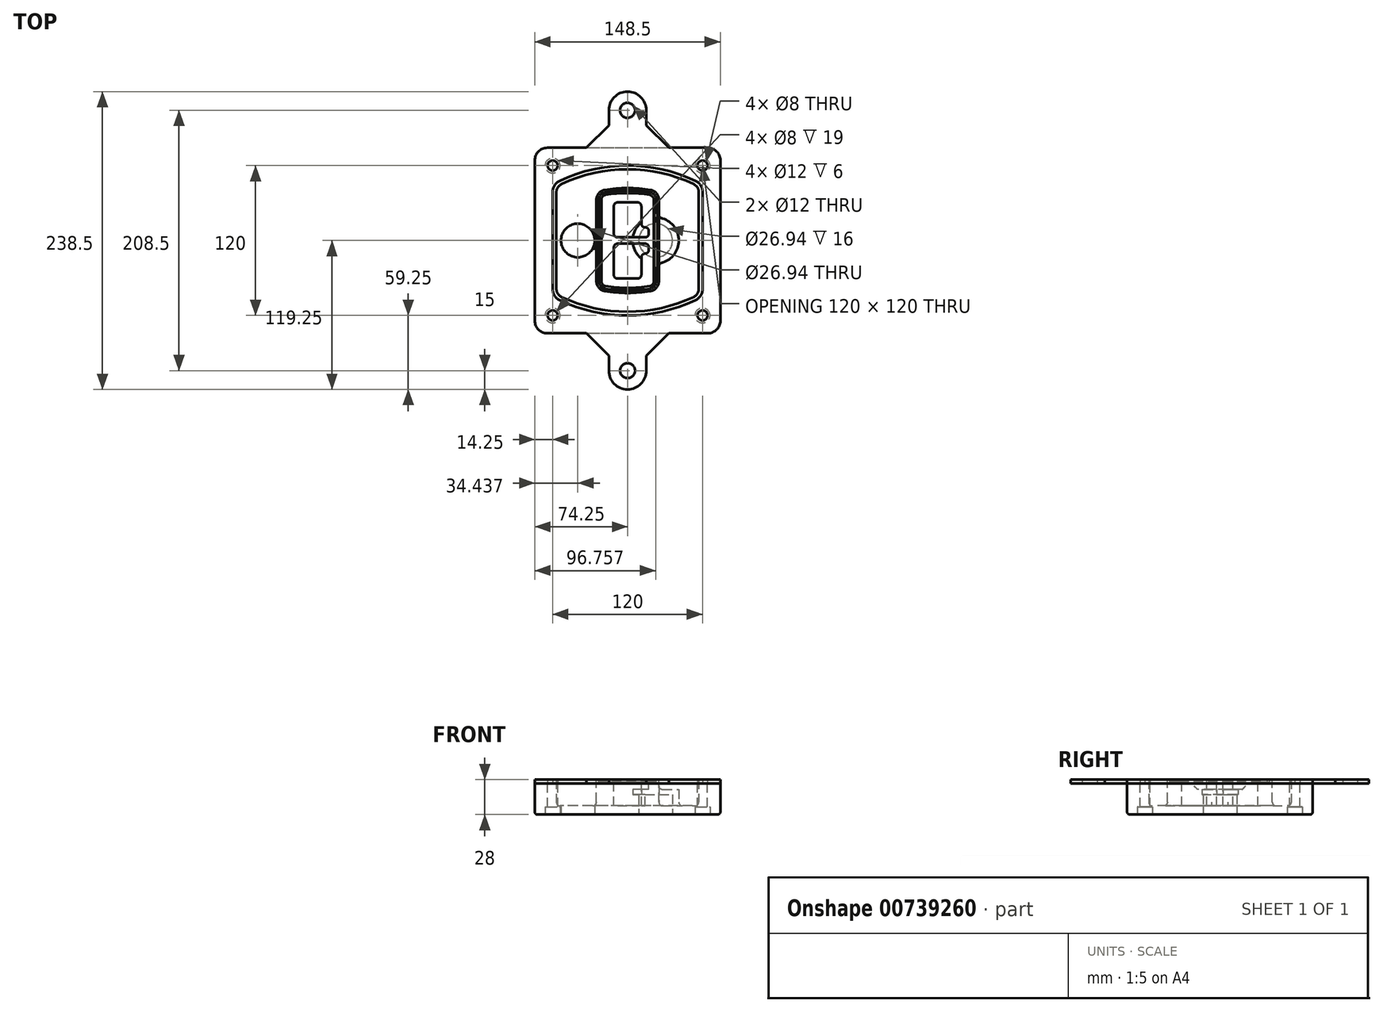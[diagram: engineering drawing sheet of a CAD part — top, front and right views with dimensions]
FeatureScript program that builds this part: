
annotation { "Feature Type Name" : "Feature", "Feature Type Description" : "" }
export const myFeature = defineFeature(function(context is Context, id is Id, definition is map)
    precondition{}
    {
        {
            var Q0;
            Q0=qCreatedBy(makeId("Top.planeOp"),FACE);
            var sketch = newSketch(context, id + "F0", { "sketchPlane" : qUnion([Q0])});
            skPoint(sketch, "E0.rect.middle", {"position": v(0, 0) * mm});
            skLineSegment(sketch, "E1.bottom", {"start": v(-64.25, -74.25) * mm, "end": v(64.25, -74.25) * mm});
            skLineSegment(sketch, "E1.top", {"start": v(-64.25, 74.25) * mm, "end": v(64.25, 74.25) * mm});
            skLineSegment(sketch, "E1.left", {"start": v(-74.25, -64.25) * mm, "end": v(-74.25, 64.25) * mm});
            skLineSegment(sketch, "E1.right", {"start": v(74.25, -64.25) * mm, "end": v(74.25, 64.25) * mm});
            skLineSegment(sketch, "E2", {"start": v(-74.25, 74.25) * mm, "end": v(74.25, -74.25) * mm, "construction": true});
            skLineSegment(sketch, "E3", {"start": v(74.25, 74.25) * mm, "end": v(-74.25, -74.25) * mm, "construction": true});
            skCircle(sketch, "E4", {"center": v(-60, 60) * mm, "radius": 4 * mm});
            skCircle(sketch, "E5", {"center": v(60, 60) * mm, "radius": 4 * mm});
            skCircle(sketch, "E6", {"center": v(60, -60) * mm, "radius": 4 * mm});
            skCircle(sketch, "E7", {"center": v(-60, -60) * mm, "radius": 4 * mm});
            skLineSegment(sketch, "E8", {"start": v(-60, 60) * mm, "end": v(60, 60) * mm, "construction": true});
            skLineSegment(sketch, "E9", {"start": v(60, 60) * mm, "end": v(60, -60) * mm, "construction": true});
            skLineSegment(sketch, "E10", {"start": v(60, -60) * mm, "end": v(-60, -60) * mm, "construction": true});
            skLineSegment(sketch, "E11", {"start": v(-60, -60) * mm, "end": v(-60, 60) * mm, "construction": true});
            skLineSegment(sketch, "E12", {"start": v(-60, 38.83) * mm, "end": v(-60, -38.83) * mm});
            skLineSegment(sketch, "E13", {"start": v(60, 38.83) * mm, "end": v(60, -38.83) * mm});
            skArc(sketch, "E14", {"start": v(54.26, 47.88) * mm, "mid": v(0, 60) * mm, "end": v(-54.26, 47.88) * mm});
            skArc(sketch, "E15", {"start": v(-54.26, -47.88) * mm, "mid": v(0, -60) * mm, "end": v(54.26, -47.88) * mm});
            skLineSegment(sketch, "E16", {"start": v(-60, 0) * mm, "end": v(60, 0) * mm, "construction": true});
            skPoint(sketch, "E17.visualSharp", {"position": v(-60, -45) * mm});
            skArc(sketch, "E17.filletArc", {"start": v(-60, -38.83) * mm, "mid": v(-58.44, -44.2) * mm, "end": v(-54.26, -47.88) * mm});
            skPoint(sketch, "E18.visualSharp", {"position": v(-60, 45) * mm});
            skArc(sketch, "E18.filletArc", {"start": v(-54.26, 47.88) * mm, "mid": v(-58.44, 44.2) * mm, "end": v(-60, 38.83) * mm});
            skPoint(sketch, "E19.visualSharp", {"position": v(60, 45) * mm});
            skArc(sketch, "E19.filletArc", {"start": v(60, 38.83) * mm, "mid": v(58.44, 44.2) * mm, "end": v(54.26, 47.88) * mm});
            skPoint(sketch, "E20.visualSharp", {"position": v(60, -45) * mm});
            skArc(sketch, "E20.filletArc", {"start": v(54.26, -47.88) * mm, "mid": v(58.44, -44.2) * mm, "end": v(60, -38.83) * mm});
            skPoint(sketch, "E21.visualSharp", {"position": v(-74.25, 74.25) * mm});
            skArc(sketch, "E21.filletArc", {"start": v(-64.25, 74.25) * mm, "mid": v(-71.32, 71.32) * mm, "end": v(-74.25, 64.25) * mm});
            skPoint(sketch, "E22.visualSharp", {"position": v(74.25, 74.25) * mm});
            skArc(sketch, "E22.filletArc", {"start": v(74.25, 64.25) * mm, "mid": v(71.32, 71.32) * mm, "end": v(64.25, 74.25) * mm});
            skPoint(sketch, "E23.visualSharp", {"position": v(74.25, -74.25) * mm});
            skArc(sketch, "E23.filletArc", {"start": v(64.25, -74.25) * mm, "mid": v(71.32, -71.32) * mm, "end": v(74.25, -64.25) * mm});
            skPoint(sketch, "E24.visualSharp", {"position": v(-74.25, -74.25) * mm});
            skArc(sketch, "E24.filletArc", {"start": v(-74.25, -64.25) * mm, "mid": v(-71.32, -71.32) * mm, "end": v(-64.25, -74.25) * mm});
            skArc(sketch, "E25.0", {"start": v(57, 38.83) * mm, "mid": v(55.9, 42.58) * mm, "end": v(52.98, 45.17) * mm});
            skLineSegment(sketch, "E25.1", {"start": v(57, 38.83) * mm, "end": v(57, -38.83) * mm});
            skArc(sketch, "E25.2", {"start": v(52.98, -45.17) * mm, "mid": v(55.9, -42.58) * mm, "end": v(57, -38.83) * mm});
            skArc(sketch, "E25.3", {"start": v(-52.98, -45.17) * mm, "mid": v(0, -57) * mm, "end": v(52.98, -45.17) * mm});
            skArc(sketch, "E25.4", {"start": v(-57, -38.83) * mm, "mid": v(-55.9, -42.58) * mm, "end": v(-52.98, -45.17) * mm});
            skArc(sketch, "E25.5", {"start": v(52.98, 45.17) * mm, "mid": v(0, 57) * mm, "end": v(-52.98, 45.17) * mm});
            skLineSegment(sketch, "E25.6", {"start": v(-57, 38.83) * mm, "end": v(-57, -38.83) * mm});
            skArc(sketch, "E25.7", {"start": v(-52.98, 45.17) * mm, "mid": v(-55.9, 42.58) * mm, "end": v(-57, 38.83) * mm});
            skArc(sketch, "E26.0", {"start": v(-55.96, 51.5) * mm, "mid": v(-61.82, 46.33) * mm, "end": v(-64, 38.83) * mm});
            skArc(sketch, "E26.1", {"start": v(55.96, 51.5) * mm, "mid": v(0, 64) * mm, "end": v(-55.96, 51.5) * mm});
            skArc(sketch, "E26.2", {"start": v(64, 38.83) * mm, "mid": v(61.82, 46.33) * mm, "end": v(55.96, 51.5) * mm});
            skLineSegment(sketch, "E26.3", {"start": v(64, 38.83) * mm, "end": v(64, -38.83) * mm});
            skArc(sketch, "E26.4", {"start": v(55.96, -51.5) * mm, "mid": v(61.82, -46.33) * mm, "end": v(64, -38.83) * mm});
            skLineSegment(sketch, "E26.5", {"start": v(-64, 38.83) * mm, "end": v(-64, -38.83) * mm});
            skArc(sketch, "E26.6", {"start": v(-55.96, -51.5) * mm, "mid": v(0, -64) * mm, "end": v(55.96, -51.5) * mm});
            skArc(sketch, "E26.7", {"start": v(-64, -38.83) * mm, "mid": v(-61.82, -46.33) * mm, "end": v(-55.96, -51.5) * mm});
            skSolve(sketch);
        }
        {
            var Q0;
            Q0=makeQuery(id+"F0.imprint","IMPRINT",FACE,{"disambiguationData":[TD([[makeQuery(id+"F0.imprint","IMPRINT",EDGE,{"derivedFrom":sQuery(id+"F0.wireOp",EDGE,"E1.bottom")}),1.0]])]});
            var Q1;
            Q1=makeQuery(id+"F0.imprint","IMPRINT",FACE,{"disambiguationData":[TD([[makeQuery(id+"F0.imprint","IMPRINT",EDGE,{"derivedFrom":sQuery(id+"F0.wireOp",EDGE,"E12")}),1.0]])]});
            var Q2;
            Q2=makeQuery(id+"F0.imprint","IMPRINT",FACE,{"disambiguationData":[TD([[makeQuery(id+"F0.imprint","IMPRINT",EDGE,{"derivedFrom":sQuery(id+"F0.wireOp",EDGE,"E25.0")}),1.0]])]});
            var Q3;
            Q3=makeQuery(id+"F0.imprint","IMPRINT",FACE,{"disambiguationData":[TD([[makeQuery(id+"F0.imprint","IMPRINT",EDGE,{"derivedFrom":sQuery(id+"F0.wireOp",EDGE,"E12")}),-1.0]])]});
            extrude(context, id + "F1", {"entities" : qUnion([Q0, Q1, Q2, Q3]), "oppositeDirection" : true, "depth" : 25 * mm});
        }
        {
            var Q0;
            Q0=makeQuery(id+"F0.imprint","IMPRINT",FACE,{"disambiguationData":[TD([[makeQuery(id+"F0.imprint","IMPRINT",EDGE,{"derivedFrom":sQuery(id+"F0.wireOp",EDGE,"E12")}),1.0]])]});
            extrude(context, id + "F2", {"entities" : qUnion([Q0]), "operationType" : NewBodyOperationType.ADD, "depth" : 3 * mm, "offsetDistance" : 25 * mm});
        }
        {
            var Q0;
            Q0=makeQuery(id+"F0.imprint","IMPRINT",FACE,{"disambiguationData":[TD([[makeQuery(id+"F0.imprint","IMPRINT",EDGE,{"derivedFrom":sQuery(id+"F0.wireOp",EDGE,"E25.0")}),1.0]])]});
            extrude(context, id + "F3", {"entities" : qUnion([Q0]), "operationType" : NewBodyOperationType.REMOVE, "oppositeDirection" : true, "depth" : 18 * mm});
        }
        {
            var Q0;
            Q0=makeQuery(id+"F2.opExtrude","CAP_FACE",FACE,{"disambiguationData":[OSD([sQuery(id+"F0.wireOp",EDGE,"E12"),sQuery(id+"F0.wireOp",EDGE,"E13"),sQuery(id+"F0.wireOp",EDGE,"E14"),sQuery(id+"F0.wireOp",EDGE,"E15"),sQuery(id+"F0.wireOp",EDGE,"E17.filletArc"),sQuery(id+"F0.wireOp",EDGE,"E18.filletArc"),sQuery(id+"F0.wireOp",EDGE,"E19.filletArc"),sQuery(id+"F0.wireOp",EDGE,"E20.filletArc"),sQuery(id+"F0.wireOp",EDGE,"E25.0"),sQuery(id+"F0.wireOp",EDGE,"E25.1"),sQuery(id+"F0.wireOp",EDGE,"E25.2"),sQuery(id+"F0.wireOp",EDGE,"E25.3"),sQuery(id+"F0.wireOp",EDGE,"E25.4"),sQuery(id+"F0.wireOp",EDGE,"E25.5"),sQuery(id+"F0.wireOp",EDGE,"E25.6"),sQuery(id+"F0.wireOp",EDGE,"E25.7")])],"isStart":false});
            var sketch = newSketch(context, id + "F4", { "sketchPlane" : qUnion([Q0])});
            skArc(sketch, "E27.0", {"start": v(-18.34, -40.45) * mm, "mid": v(0, -42) * mm, "end": v(18.34, -40.45) * mm});
            skArc(sketch, "E28.0", {"start": v(18.34, 40.45) * mm, "mid": v(0, 42) * mm, "end": v(-18.34, 40.45) * mm});
            skLineSegment(sketch, "E29", {"start": v(-25, 32.57) * mm, "end": v(-25, -32.57) * mm});
            skLineSegment(sketch, "E30", {"start": v(25, 32.57) * mm, "end": v(25, -32.57) * mm});
            skLineSegment(sketch, "E31", {"start": v(-25, 39.1) * mm, "end": v(25, 39.1) * mm, "construction": true});
            skLineSegment(sketch, "E32", {"start": v(-25, -39.1) * mm, "end": v(25, -39.1) * mm, "construction": true});
            skPoint(sketch, "E33.visualSharp", {"position": v(-25, 39.1) * mm});
            skArc(sketch, "E33.filletArc", {"start": v(-18.34, 40.45) * mm, "mid": v(-23.11, 37.73) * mm, "end": v(-25, 32.57) * mm});
            skPoint(sketch, "E34.visualSharp", {"position": v(25, 39.1) * mm});
            skArc(sketch, "E34.filletArc", {"start": v(25, 32.57) * mm, "mid": v(23.11, 37.73) * mm, "end": v(18.34, 40.45) * mm});
            skPoint(sketch, "E35.visualSharp", {"position": v(25, -39.1) * mm});
            skArc(sketch, "E35.filletArc", {"start": v(18.34, -40.45) * mm, "mid": v(23.11, -37.73) * mm, "end": v(25, -32.57) * mm});
            skPoint(sketch, "E36.visualSharp", {"position": v(-25, -39.1) * mm});
            skArc(sketch, "E36.filletArc", {"start": v(-25, -32.57) * mm, "mid": v(-23.11, -37.73) * mm, "end": v(-18.34, -40.45) * mm});
            skArc(sketch, "E37.0", {"start": v(52.98, 45.17) * mm, "mid": v(0, 57) * mm, "end": v(-52.98, 45.17) * mm});
            skArc(sketch, "E37.1", {"start": v(-52.98, 45.17) * mm, "mid": v(-55.9, 42.58) * mm, "end": v(-57, 38.83) * mm});
            skLineSegment(sketch, "E37.2", {"start": v(-57, 38.83) * mm, "end": v(-57, -38.83) * mm});
            skArc(sketch, "E37.3", {"start": v(-57, -38.83) * mm, "mid": v(-55.9, -42.58) * mm, "end": v(-52.98, -45.17) * mm});
            skArc(sketch, "E37.4", {"start": v(-52.98, -45.17) * mm, "mid": v(0, -57) * mm, "end": v(52.98, -45.17) * mm});
            skArc(sketch, "E37.5", {"start": v(52.98, -45.17) * mm, "mid": v(55.9, -42.58) * mm, "end": v(57, -38.83) * mm});
            skLineSegment(sketch, "E37.6", {"start": v(57, 38.83) * mm, "end": v(57, -38.83) * mm});
            skArc(sketch, "E37.7", {"start": v(57, 38.83) * mm, "mid": v(55.9, 42.58) * mm, "end": v(52.98, 45.17) * mm});
            skLineSegment(sketch, "E38.0", {"start": v(23, 32.57) * mm, "end": v(23, -32.57) * mm});
            skArc(sketch, "E38.1", {"start": v(18, -38.48) * mm, "mid": v(21.58, -36.44) * mm, "end": v(23, -32.57) * mm});
            skArc(sketch, "E38.2", {"start": v(-18, -38.48) * mm, "mid": v(0, -40) * mm, "end": v(18, -38.48) * mm});
            skArc(sketch, "E38.3", {"start": v(-23, -32.57) * mm, "mid": v(-21.58, -36.44) * mm, "end": v(-18, -38.48) * mm});
            skLineSegment(sketch, "E38.4", {"start": v(-23, 32.57) * mm, "end": v(-23, -32.57) * mm});
            skArc(sketch, "E38.5", {"start": v(23, 32.57) * mm, "mid": v(21.58, 36.44) * mm, "end": v(18, 38.48) * mm});
            skArc(sketch, "E38.6", {"start": v(-18, 38.48) * mm, "mid": v(-21.58, 36.44) * mm, "end": v(-23, 32.57) * mm});
            skArc(sketch, "E38.7", {"start": v(18, 38.48) * mm, "mid": v(0, 40) * mm, "end": v(-18, 38.48) * mm});
            skArc(sketch, "E39.0", {"start": v(21, 32.57) * mm, "mid": v(20.06, 35.15) * mm, "end": v(17.67, 36.5) * mm});
            skLineSegment(sketch, "E39.1", {"start": v(21, 32.57) * mm, "end": v(21, -32.57) * mm});
            skArc(sketch, "E39.2", {"start": v(17.67, -36.5) * mm, "mid": v(20.06, -35.15) * mm, "end": v(21, -32.57) * mm});
            skArc(sketch, "E39.3", {"start": v(-17.67, -36.5) * mm, "mid": v(0, -38) * mm, "end": v(17.67, -36.5) * mm});
            skArc(sketch, "E39.4", {"start": v(-21, -32.57) * mm, "mid": v(-20.06, -35.15) * mm, "end": v(-17.67, -36.5) * mm});
            skArc(sketch, "E39.5", {"start": v(17.67, 36.5) * mm, "mid": v(0, 38) * mm, "end": v(-17.67, 36.5) * mm});
            skLineSegment(sketch, "E39.6", {"start": v(-21, 32.57) * mm, "end": v(-21, -32.57) * mm});
            skArc(sketch, "E39.7", {"start": v(-17.67, 36.5) * mm, "mid": v(-20.06, 35.15) * mm, "end": v(-21, 32.57) * mm});
            skLineSegment(sketch, "E40", {"start": v(-25, 0) * mm, "end": v(25, 0) * mm, "construction": true});
            skLineSegment(sketch, "E41", {"start": v(-11, 5.5) * mm, "end": v(-11, 27.5) * mm});
            skLineSegment(sketch, "E42", {"start": v(-8, 30.5) * mm, "end": v(8, 30.5) * mm});
            skLineSegment(sketch, "E43", {"start": v(11, 27.5) * mm, "end": v(11, 13.5) * mm});
            skLineSegment(sketch, "E44", {"start": v(14, 10.5) * mm, "end": v(14, 10.5) * mm});
            skLineSegment(sketch, "E45", {"start": v(17, 7.5) * mm, "end": v(17, 5.5) * mm});
            skLineSegment(sketch, "E46", {"start": v(14, 2.5) * mm, "end": v(-8, 2.5) * mm});
            skPoint(sketch, "E47.visualSharp", {"position": v(-11, 30.5) * mm});
            skArc(sketch, "E47.filletArc", {"start": v(-8, 30.5) * mm, "mid": v(-10.12, 29.62) * mm, "end": v(-11, 27.5) * mm});
            skPoint(sketch, "E48.visualSharp", {"position": v(11, 30.5) * mm});
            skArc(sketch, "E48.filletArc", {"start": v(11, 27.5) * mm, "mid": v(10.12, 29.62) * mm, "end": v(8, 30.5) * mm});
            skPoint(sketch, "E49.visualSharp", {"position": v(11, 10.5) * mm});
            skArc(sketch, "E49.filletArc", {"start": v(11, 13.5) * mm, "mid": v(11.88, 11.38) * mm, "end": v(14, 10.5) * mm});
            skPoint(sketch, "E50.visualSharp", {"position": v(17, 10.5) * mm});
            skArc(sketch, "E50.filletArc", {"start": v(17, 7.5) * mm, "mid": v(16.12, 9.62) * mm, "end": v(14, 10.5) * mm});
            skPoint(sketch, "E51.visualSharp", {"position": v(17, 2.5) * mm});
            skArc(sketch, "E51.filletArc", {"start": v(14, 2.5) * mm, "mid": v(16.12, 3.38) * mm, "end": v(17, 5.5) * mm});
            skPoint(sketch, "E52.visualSharp", {"position": v(-11, 2.5) * mm});
            skArc(sketch, "E52.filletArc", {"start": v(-11, 5.5) * mm, "mid": v(-10.12, 3.38) * mm, "end": v(-8, 2.5) * mm});
            skLineSegment(sketch, "E53.0.MirrorCS", {"start": v(14, -2.5) * mm, "end": v(-8, -2.5) * mm});
            skArc(sketch, "E54.0.MirrorCS", {"start": v(-11, -5.5) * mm, "mid": v(-10.12, -3.38) * mm, "end": v(-8, -2.5) * mm});
            skLineSegment(sketch, "E55.0.MirrorCS", {"start": v(-11, -5.5) * mm, "end": v(-11, -27.5) * mm});
            skArc(sketch, "E56.0.MirrorCS", {"start": v(-8, -30.5) * mm, "mid": v(-10.12, -29.62) * mm, "end": v(-11, -27.5) * mm});
            skLineSegment(sketch, "E57.0.MirrorCS", {"start": v(-8, -30.5) * mm, "end": v(8, -30.5) * mm});
            skArc(sketch, "E58.0.MirrorCS", {"start": v(11, -27.5) * mm, "mid": v(10.12, -29.62) * mm, "end": v(8, -30.5) * mm});
            skLineSegment(sketch, "E59.0.MirrorCS", {"start": v(11, -27.5) * mm, "end": v(11, -13.5) * mm});
            skArc(sketch, "E60.0.MirrorCS", {"start": v(11, -13.5) * mm, "mid": v(11.88, -11.38) * mm, "end": v(14, -10.5) * mm});
            skArc(sketch, "E61.0.MirrorCS", {"start": v(17, -7.5) * mm, "mid": v(16.12, -9.62) * mm, "end": v(14, -10.5) * mm});
            skLineSegment(sketch, "E62.0.MirrorCS", {"start": v(17, -7.5) * mm, "end": v(17, -5.5) * mm});
            skArc(sketch, "E63.0.MirrorCS", {"start": v(14, -2.5) * mm, "mid": v(16.12, -3.38) * mm, "end": v(17, -5.5) * mm});
            skSolve(sketch);
        }
        {
            var Q0;
            Q0=makeQuery(id+"F4.imprint","IMPRINT",FACE,{"disambiguationData":[TD([[makeQuery(id+"F4.imprint","IMPRINT",EDGE,{"derivedFrom":sQuery(id+"F4.wireOp",EDGE,"E27.0")}),1.0]])]});
            var Q1;
            Q1=makeQuery(id+"F4.imprint","IMPRINT",FACE,{"disambiguationData":[TD([[makeQuery(id+"F4.imprint","IMPRINT",EDGE,{"derivedFrom":sQuery(id+"F4.wireOp",EDGE,"E38.0")}),-1.0]])]});
            var Q2;
            Q2=makeQuery(id+"F4.imprint","IMPRINT",FACE,{"disambiguationData":[TD([[makeQuery(id+"F4.imprint","IMPRINT",EDGE,{"derivedFrom":sQuery(id+"F4.wireOp",EDGE,"E39.0")}),1.0]])]});
            extrude(context, id + "F5", {"entities" : qUnion([Q0, Q1, Q2]), "operationType" : NewBodyOperationType.ADD, "endBound" : BoundingType.UP_TO_NEXT, "oppositeDirection" : true, "depth" : 25 * mm});
        }
        {
            var Q0;
            Q0=makeQuery(id+"F4.imprint","IMPRINT",FACE,{"disambiguationData":[TD([[makeQuery(id+"F4.imprint","IMPRINT",EDGE,{"derivedFrom":sQuery(id+"F4.wireOp",EDGE,"E38.0")}),-1.0]])]});
            extrude(context, id + "F6", {"entities" : qUnion([Q0]), "operationType" : NewBodyOperationType.REMOVE, "oppositeDirection" : true, "depth" : 2 * mm});
        }
        {
            var Q0;
            Q0=makeQuery(id+"F1.opExtrude","CAP_FACE",FACE,{"disambiguationData":[OSD([sQuery(id+"F0.wireOp",EDGE,"E1.bottom"),sQuery(id+"F0.wireOp",EDGE,"E1.top"),sQuery(id+"F0.wireOp",EDGE,"E1.left"),sQuery(id+"F0.wireOp",EDGE,"E1.right"),sQuery(id+"F0.wireOp",EDGE,"E4"),sQuery(id+"F0.wireOp",EDGE,"E5"),sQuery(id+"F0.wireOp",EDGE,"E6"),sQuery(id+"F0.wireOp",EDGE,"E7"),sQuery(id+"F0.wireOp",EDGE,"E21.filletArc"),sQuery(id+"F0.wireOp",EDGE,"E22.filletArc"),sQuery(id+"F0.wireOp",EDGE,"E23.filletArc"),sQuery(id+"F0.wireOp",EDGE,"E24.filletArc")])],"isStart":false});
            var sketch = newSketch(context, id + "F7", { "sketchPlane" : qUnion([Q0])});
            skCircle(sketch, "E64", {"center": v(22.5, 0) * mm, "radius": 13.47 * mm});
            skCircle(sketch, "E65", {"center": v(-39.81, 0) * mm, "radius": 13.47 * mm});
            skLineSegment(sketch, "E66", {"start": v(74.25, 0) * mm, "end": v(-74.25, 0) * mm});
            skCircle(sketch, "E67", {"center": v(22.5, 0) * mm, "radius": 18.47 * mm});
            skCircle(sketch, "E68", {"center": v(60, -60) * mm, "radius": 6 * mm});
            skCircle(sketch, "E69", {"center": v(-60, -60) * mm, "radius": 6 * mm});
            skCircle(sketch, "E70", {"center": v(-60, 60) * mm, "radius": 6 * mm});
            skCircle(sketch, "E71", {"center": v(60, 60) * mm, "radius": 6 * mm});
            skSolve(sketch);
        }
        {
            var Q0;
            {var subQ1=sQuery(id+"F7.wireOp",EDGE,"E66");var subQ4=sQuery(id+"F7.wireOp",EDGE,"E64");var subQ6=makeQuery(id+"F7.imprint","INTERSECT",VERTEX,{"disambiguationData":[OD(0.0)],"derivedFrom":[subQ4,subQ1]});Q0=makeQuery(id+"F7.imprint","IMPRINT",FACE,{"disambiguationData":[TD([[makeQuery(id+"F7.imprint","IMPRINT",EDGE,{"disambiguationData":[TD([[subQ6,-1.0]])],"derivedFrom":subQ4}),-1.0]])]});}
            var Q1;
            {var subQ0=sQuery(id+"F7.wireOp",EDGE,"E66");var subQ1=sQuery(id+"F7.wireOp",EDGE,"E64");var subQ3=makeQuery(id+"F7.imprint","INTERSECT",VERTEX,{"disambiguationData":[OD(0.0)],"derivedFrom":[subQ1,subQ0]});Q1=makeQuery(id+"F7.imprint","IMPRINT",FACE,{"disambiguationData":[TD([[makeQuery(id+"F7.imprint","IMPRINT",EDGE,{"disambiguationData":[TD([[subQ3,-1.0]])],"derivedFrom":subQ1}),1.0]])]});}
            var Q2;
            {var subQ0=sQuery(id+"F7.wireOp",EDGE,"E66");var subQ1=sQuery(id+"F7.wireOp",EDGE,"E64");var subQ3=makeQuery(id+"F7.imprint","INTERSECT",VERTEX,{"disambiguationData":[OD(0.0)],"derivedFrom":[subQ1,subQ0]});Q2=makeQuery(id+"F7.imprint","IMPRINT",FACE,{"disambiguationData":[TD([[makeQuery(id+"F7.imprint","IMPRINT",EDGE,{"disambiguationData":[TD([[subQ3,1.0]])],"derivedFrom":subQ1}),1.0]])]});}
            var Q3;
            {var subQ1=sQuery(id+"F7.wireOp",EDGE,"E66");var subQ4=sQuery(id+"F7.wireOp",EDGE,"E64");var subQ6=makeQuery(id+"F7.imprint","INTERSECT",VERTEX,{"disambiguationData":[OD(0.0)],"derivedFrom":[subQ4,subQ1]});Q3=makeQuery(id+"F7.imprint","IMPRINT",FACE,{"disambiguationData":[TD([[makeQuery(id+"F7.imprint","IMPRINT",EDGE,{"disambiguationData":[TD([[subQ6,1.0]])],"derivedFrom":subQ4}),-1.0]])]});}
            extrude(context, id + "F8", {"entities" : qUnion([Q0, Q1, Q2, Q3]), "operationType" : NewBodyOperationType.ADD, "oppositeDirection" : true, "depth" : 20 * mm});
        }
        {
            var Q0;
            {var subQ0=sQuery(id+"F7.wireOp",EDGE,"E66");var subQ1=sQuery(id+"F7.wireOp",EDGE,"E64");var subQ3=makeQuery(id+"F7.imprint","INTERSECT",VERTEX,{"disambiguationData":[OD(0.0)],"derivedFrom":[subQ1,subQ0]});Q0=makeQuery(id+"F7.imprint","IMPRINT",FACE,{"disambiguationData":[TD([[makeQuery(id+"F7.imprint","IMPRINT",EDGE,{"disambiguationData":[TD([[subQ3,-1.0]])],"derivedFrom":subQ1}),1.0]])]});}
            var Q1;
            {var subQ0=sQuery(id+"F7.wireOp",EDGE,"E66");var subQ1=sQuery(id+"F7.wireOp",EDGE,"E64");var subQ3=makeQuery(id+"F7.imprint","INTERSECT",VERTEX,{"disambiguationData":[OD(0.0)],"derivedFrom":[subQ1,subQ0]});Q1=makeQuery(id+"F7.imprint","IMPRINT",FACE,{"disambiguationData":[TD([[makeQuery(id+"F7.imprint","IMPRINT",EDGE,{"disambiguationData":[TD([[subQ3,1.0]])],"derivedFrom":subQ1}),1.0]])]});}
            extrude(context, id + "F9", {"entities" : qUnion([Q0, Q1]), "operationType" : NewBodyOperationType.REMOVE, "oppositeDirection" : true, "depth" : 16 * mm});
        }
        {
            var Q0;
            {var subQ0=sQuery(id+"F7.wireOp",EDGE,"E66");var subQ1=sQuery(id+"F7.wireOp",EDGE,"E65");var subQ3=makeQuery(id+"F7.imprint","INTERSECT",VERTEX,{"disambiguationData":[OD(0.0)],"derivedFrom":[subQ1,subQ0]});Q0=makeQuery(id+"F7.imprint","IMPRINT",FACE,{"disambiguationData":[TD([[makeQuery(id+"F7.imprint","IMPRINT",EDGE,{"disambiguationData":[TD([[subQ3,-1.0]])],"derivedFrom":subQ1}),1.0]])]});}
            var Q1;
            {var subQ0=sQuery(id+"F7.wireOp",EDGE,"E66");var subQ1=sQuery(id+"F7.wireOp",EDGE,"E65");var subQ3=makeQuery(id+"F7.imprint","INTERSECT",VERTEX,{"disambiguationData":[OD(0.0)],"derivedFrom":[subQ1,subQ0]});Q1=makeQuery(id+"F7.imprint","IMPRINT",FACE,{"disambiguationData":[TD([[makeQuery(id+"F7.imprint","IMPRINT",EDGE,{"disambiguationData":[TD([[subQ3,1.0]])],"derivedFrom":subQ1}),1.0]])]});}
            extrude(context, id + "F10", {"entities" : qUnion([Q0, Q1]), "operationType" : NewBodyOperationType.REMOVE, "oppositeDirection" : true, "depth" : 25 * mm});
        }
        {
            var Q0;
            Q0=makeQuery(id+"F7.imprint","IMPRINT",FACE,{"disambiguationData":[TD([[makeQuery(id+"F7.imprint","IMPRINT",EDGE,{"derivedFrom":sQuery(id+"F7.wireOp",EDGE,"E68")}),1.0]])]});
            var Q1;
            Q1=makeQuery(id+"F7.imprint","IMPRINT",FACE,{"disambiguationData":[TD([[makeQuery(id+"F7.imprint","IMPRINT",EDGE,{"derivedFrom":makeQuery(id+"F1.opExtrude","CAP_EDGE",EDGE,{"disambiguationData":[OSD([sQuery(id+"F0.wireOp",EDGE,"E5")])],"isStart":false})}),-1.0]])]});
            var Q2;
            Q2=makeQuery(id+"F7.imprint","IMPRINT",FACE,{"disambiguationData":[TD([[makeQuery(id+"F7.imprint","IMPRINT",EDGE,{"derivedFrom":sQuery(id+"F7.wireOp",EDGE,"E69")}),1.0]])]});
            var Q3;
            Q3=makeQuery(id+"F7.imprint","IMPRINT",FACE,{"disambiguationData":[TD([[makeQuery(id+"F7.imprint","IMPRINT",EDGE,{"derivedFrom":makeQuery(id+"F1.opExtrude","CAP_EDGE",EDGE,{"disambiguationData":[OSD([sQuery(id+"F0.wireOp",EDGE,"E4")])],"isStart":false})}),-1.0]])]});
            var Q4;
            Q4=makeQuery(id+"F7.imprint","IMPRINT",FACE,{"disambiguationData":[TD([[makeQuery(id+"F7.imprint","IMPRINT",EDGE,{"derivedFrom":sQuery(id+"F7.wireOp",EDGE,"E70")}),1.0]])]});
            var Q5;
            Q5=makeQuery(id+"F7.imprint","IMPRINT",FACE,{"disambiguationData":[TD([[makeQuery(id+"F7.imprint","IMPRINT",EDGE,{"derivedFrom":makeQuery(id+"F1.opExtrude","CAP_EDGE",EDGE,{"disambiguationData":[OSD([sQuery(id+"F0.wireOp",EDGE,"E7")])],"isStart":false})}),-1.0]])]});
            var Q6;
            Q6=makeQuery(id+"F7.imprint","IMPRINT",FACE,{"disambiguationData":[TD([[makeQuery(id+"F7.imprint","IMPRINT",EDGE,{"derivedFrom":sQuery(id+"F7.wireOp",EDGE,"E71")}),1.0]])]});
            var Q7;
            Q7=makeQuery(id+"F7.imprint","IMPRINT",FACE,{"disambiguationData":[TD([[makeQuery(id+"F7.imprint","IMPRINT",EDGE,{"derivedFrom":makeQuery(id+"F1.opExtrude","CAP_EDGE",EDGE,{"disambiguationData":[OSD([sQuery(id+"F0.wireOp",EDGE,"E6")])],"isStart":false})}),-1.0]])]});
            extrude(context, id + "F11", {"entities" : qUnion([Q0, Q1, Q2, Q3, Q4, Q5, Q6, Q7]), "operationType" : NewBodyOperationType.REMOVE, "oppositeDirection" : true, "depth" : 6 * mm});
        }
        {
            var Q0;
            Q0=makeQuery(id+"F9.boolean.opBoolean","COPY",FACE,{"derivedFrom":makeQuery(id+"F9.opExtrude","CAP_FACE",FACE,{"disambiguationData":[OSD([sQuery(id+"F7.wireOp",EDGE,"E64")])],"isStart":false})});
            var sketch = newSketch(context, id + "F12", { "sketchPlane" : qUnion([Q0])});
            skArc(sketch, "E72.0", {"start": v(11, 14.45) * mm, "mid": v(6.45, 9.13) * mm, "end": v(4.2, 2.5) * mm});
            skArc(sketch, "E72.1", {"start": v(4.2, -2.5) * mm, "mid": v(6.45, -9.13) * mm, "end": v(11, -14.45) * mm});
            skLineSegment(sketch, "E73", {"start": v(4.2, -2.5) * mm, "end": v(14, -2.5) * mm});
            skLineSegment(sketch, "E74.0", {"start": v(14, 2.5) * mm, "end": v(4.2, 2.5) * mm});
            skArc(sketch, "E74.1", {"start": v(14, 2.5) * mm, "mid": v(16.12, 3.38) * mm, "end": v(17, 5.5) * mm});
            skLineSegment(sketch, "E74.2", {"start": v(17, 7.5) * mm, "end": v(17, 5.5) * mm});
            skArc(sketch, "E74.3", {"start": v(17, 7.5) * mm, "mid": v(16.12, 9.62) * mm, "end": v(14, 10.5) * mm});
            skArc(sketch, "E74.4", {"start": v(11, 13.5) * mm, "mid": v(11.88, 11.38) * mm, "end": v(14, 10.5) * mm});
            skLineSegment(sketch, "E74.5", {"start": v(11, 14.45) * mm, "end": v(11, 13.5) * mm});
            skLineSegment(sketch, "E74.7", {"start": v(14, -2.5) * mm, "end": v(4.2, -2.5) * mm});
            skArc(sketch, "E74.8", {"start": v(14, -2.5) * mm, "mid": v(16.12, -3.38) * mm, "end": v(17, -5.5) * mm});
            skLineSegment(sketch, "E74.9", {"start": v(17, -7.5) * mm, "end": v(17, -5.5) * mm});
            skArc(sketch, "E74.10", {"start": v(17, -7.5) * mm, "mid": v(16.12, -9.62) * mm, "end": v(14, -10.5) * mm});
            skArc(sketch, "E74.11", {"start": v(11, -13.5) * mm, "mid": v(11.88, -11.38) * mm, "end": v(14, -10.5) * mm});
            skLineSegment(sketch, "E74.12", {"start": v(11, -14.45) * mm, "end": v(11, -13.5) * mm});
            skPoint(sketch, "E75.orphan", {"position": v(11, -27.5) * mm});
            skPoint(sketch, "E76.orphan", {"position": v(-8, -2.5) * mm});
            skPoint(sketch, "E77.orphan", {"position": v(-8, 2.5) * mm});
            skPoint(sketch, "E78.orphan", {"position": v(11, 27.5) * mm});
            skSolve(sketch);
        }
        {
            var Q0;
            {var subQ7=sQuery(id+"F12.wireOp",EDGE,"E72.0");var subQ14=sQuery(id+"F12.wireOp",EDGE,"E72.1");var subQ16=sQuery(id+"F12.wireOp",EDGE,"E74.1");var subQ18=sQuery(id+"F12.wireOp",EDGE,"E74.8");Q0=qUnion([makeQuery(id+"F12.imprint","IMPRINT",FACE,{"disambiguationData":[TD([[makeQuery(id+"F12.imprint","IMPRINT",EDGE,{"derivedFrom":subQ7}),1.0]])]}),makeQuery(id+"F12.imprint","IMPRINT",FACE,{"disambiguationData":[TD([[makeQuery(id+"F12.imprint","IMPRINT",EDGE,{"derivedFrom":subQ14}),1.0]])]}),makeQuery(id+"F12.imprint","IMPRINT",FACE,{"disambiguationData":[TD([[makeQuery(id+"F12.imprint","IMPRINT",EDGE,{"derivedFrom":subQ16}),1.0]])]}),makeQuery(id+"F12.imprint","IMPRINT",FACE,{"disambiguationData":[TD([[makeQuery(id+"F12.imprint","IMPRINT",EDGE,{"derivedFrom":subQ18}),-1.0]])]})]);}
            var Q1;
            Q1=makeQuery(id+"F5.boolean.opBoolean","SPLIT",FACE,{"disambiguationData":[TD([makeQuery(id+"F5.opExtrude","SWEPT_FACE",FACE,{"disambiguationData":[OSD([sQuery(id+"F4.wireOp",EDGE,"E41")])]})])],"derivedFrom":makeQuery(id+"F3.boolean.opBoolean","COPY",FACE,{"derivedFrom":makeQuery(id+"F3.opExtrude","CAP_FACE",FACE,{"disambiguationData":[OSD([sQuery(id+"F0.wireOp",EDGE,"E25.0"),sQuery(id+"F0.wireOp",EDGE,"E25.1"),sQuery(id+"F0.wireOp",EDGE,"E25.2"),sQuery(id+"F0.wireOp",EDGE,"E25.3"),sQuery(id+"F0.wireOp",EDGE,"E25.4"),sQuery(id+"F0.wireOp",EDGE,"E25.5"),sQuery(id+"F0.wireOp",EDGE,"E25.6"),sQuery(id+"F0.wireOp",EDGE,"E25.7")])],"isStart":false})})});
            extrude(context, id + "F13", {"entities" : qUnion([Q0]), "operationType" : NewBodyOperationType.REMOVE, "endBound" : BoundingType.UP_TO_SURFACE, "endBoundEntityFace" : qUnion([Q1]), "depth" : 25 * mm});
        }
        {
            var Q0;
            Q0=makeQuery(id+"F3.boolean.opBoolean","COPY",EDGE,{"derivedFrom":makeQuery(id+"F3.opExtrude","CAP_EDGE",EDGE,{"disambiguationData":[OSD([sQuery(id+"F0.wireOp",EDGE,"E25.6")])],"isStart":false})});
            var Q1;
            Q1=makeQuery(id+"F8.boolean.opBoolean","INTERSECT",EDGE,{"derivedFrom":[makeQuery(id+"F5.opExtrude","SWEPT_FACE",FACE,{"disambiguationData":[OSD([sQuery(id+"F4.wireOp",EDGE,"E30")])]}),makeQuery(id+"F8.opExtrude","CAP_FACE",FACE,{"disambiguationData":[OSD([sQuery(id+"F7.wireOp",EDGE,"E67")])],"isStart":false})]});
            var Q2;
            Q2=makeQuery(id+"F8.boolean.opBoolean","INTERSECT",EDGE,{"disambiguationData":[OD(1.0)],"derivedFrom":[makeQuery(id+"F5.opExtrude","SWEPT_FACE",FACE,{"disambiguationData":[OSD([sQuery(id+"F4.wireOp",EDGE,"E30")])]}),makeQuery(id+"F8.opExtrude","SWEPT_FACE",FACE,{"disambiguationData":[OSD([sQuery(id+"F7.wireOp",EDGE,"E67")])]})]});
            var Q3;
            {var subQ0=sQuery(id+"F4.wireOp",EDGE,"E30");Q3=makeQuery(id+"F8.boolean.opBoolean","SPLIT",EDGE,{"disambiguationData":[TD([makeQuery(id+"F5.opExtrude","SWEPT_FACE",FACE,{"disambiguationData":[OSD([sQuery(id+"F4.wireOp",EDGE,"E35.filletArc")])]})])],"derivedFrom":makeQuery(id+"F5.opExtrude","CAP_EDGE",EDGE,{"disambiguationData":[OSD([subQ0])],"isStart":false})});}
            var Q4;
            {var subQ0=sQuery(id+"F0.wireOp",EDGE,"E25.7");var subQ1=sQuery(id+"F0.wireOp",EDGE,"E25.1");var subQ2=sQuery(id+"F0.wireOp",EDGE,"E25.6");var subQ3=sQuery(id+"F0.wireOp",EDGE,"E25.5");var subQ4=sQuery(id+"F0.wireOp",EDGE,"E25.4");var subQ5=sQuery(id+"F0.wireOp",EDGE,"E25.0");var subQ6=sQuery(id+"F0.wireOp",EDGE,"E25.2");var subQ7=sQuery(id+"F0.wireOp",EDGE,"E25.3");Q4=makeQuery(id+"F8.boolean.opBoolean","INTERSECT",EDGE,{"derivedFrom":[makeQuery(id+"F5.boolean.opBoolean","SPLIT",FACE,{"disambiguationData":[TD([makeQuery(id+"F2.opExtrude","SWEPT_FACE",FACE,{"disambiguationData":[OSD([subQ5])]})])],"derivedFrom":makeQuery(id+"F3.boolean.opBoolean","COPY",FACE,{"derivedFrom":makeQuery(id+"F3.opExtrude","CAP_FACE",FACE,{"disambiguationData":[OSD([subQ5,subQ1,subQ6,subQ7,subQ4,subQ3,subQ2,subQ0])],"isStart":false})})}),makeQuery(id+"F8.opExtrude","SWEPT_FACE",FACE,{"disambiguationData":[OSD([sQuery(id+"F7.wireOp",EDGE,"E67")])]})]});}
            var Q5;
            Q5=makeQuery(id+"F8.boolean.opBoolean","INTERSECT",EDGE,{"disambiguationData":[OD(0.0)],"derivedFrom":[makeQuery(id+"F5.opExtrude","SWEPT_FACE",FACE,{"disambiguationData":[OSD([sQuery(id+"F4.wireOp",EDGE,"E30")])]}),makeQuery(id+"F8.opExtrude","SWEPT_FACE",FACE,{"disambiguationData":[OSD([sQuery(id+"F7.wireOp",EDGE,"E67")])]})]});
            fillet(context, id + "F14", {"entities" : qUnion([Q0, Q1, Q2, Q3, Q4, Q5]), "radius" : 3 * mm, "tangentPropagation" : true, "allowEdgeOverflow" : false});
        }
        {
            var Q0;
            Q0=makeQuery(id+"F1.opExtrude","CAP_EDGE",EDGE,{"disambiguationData":[OSD([sQuery(id+"F0.wireOp",EDGE,"E1.bottom")])],"isStart":false});
            fillet(context, id + "F15", {"entities" : qUnion([Q0]), "radius" : 2 * mm, "tangentPropagation" : true, "allowEdgeOverflow" : false});
        }
        {
            var Q0;
            {var subQ0=sQuery(id+"F0.wireOp",EDGE,"E21.filletArc");var subQ1=sQuery(id+"F0.wireOp",EDGE,"E7");var subQ2=sQuery(id+"F0.wireOp",EDGE,"E6");var subQ3=sQuery(id+"F0.wireOp",EDGE,"E5");var subQ4=sQuery(id+"F0.wireOp",EDGE,"E4");var subQ5=sQuery(id+"F0.wireOp",EDGE,"E22.filletArc");var subQ6=sQuery(id+"F0.wireOp",EDGE,"E1.bottom");var subQ7=sQuery(id+"F0.wireOp",EDGE,"E1.right");var subQ8=sQuery(id+"F0.wireOp",EDGE,"E1.top");var subQ9=sQuery(id+"F0.wireOp",EDGE,"E1.left");var subQ10=sQuery(id+"F0.wireOp",EDGE,"E23.filletArc");var subQ11=sQuery(id+"F0.wireOp",EDGE,"E24.filletArc");Q0=makeQuery(id+"F2.boolean.opBoolean","SPLIT",FACE,{"disambiguationData":[TD([makeQuery(id+"F1.opExtrude","SWEPT_FACE",FACE,{"disambiguationData":[OSD([subQ6])]})])],"derivedFrom":makeQuery(id+"F1.opExtrude","CAP_FACE",FACE,{"disambiguationData":[OSD([subQ6,subQ8,subQ9,subQ7,subQ4,subQ3,subQ2,subQ1,subQ0,subQ5,subQ10,subQ11])],"isStart":true})});}
            var sketch = newSketch(context, id + "F16", { "sketchPlane" : qUnion([Q0])});
            skCircle(sketch, "E79.0", {"center": v(-60, 60) * mm, "radius": 4 * mm});
            skCircle(sketch, "E79.1", {"center": v(60, 60) * mm, "radius": 4 * mm});
            skCircle(sketch, "E79.2", {"center": v(-60, -60) * mm, "radius": 4 * mm});
            skCircle(sketch, "E79.3", {"center": v(60, -60) * mm, "radius": 4 * mm});
            skLineSegment(sketch, "E79.4", {"start": v(-74.25, -64.25) * mm, "end": v(-74.25, 64.25) * mm});
            skLineSegment(sketch, "E79.5", {"start": v(-64.25, -74.25) * mm, "end": v(64.25, -74.25) * mm});
            skLineSegment(sketch, "E79.6", {"start": v(-64.25, 74.25) * mm, "end": v(64.25, 74.25) * mm});
            skLineSegment(sketch, "E79.7", {"start": v(74.25, -64.25) * mm, "end": v(74.25, 64.25) * mm, "construction": true});
            skPoint(sketch, "E79.9", {"position": v(-71.32, -71.32) * mm});
            skLineSegment(sketch, "E80", {"start": v(0, 74.25) * mm, "end": v(0, 104.25) * mm, "construction": true});
            skLineSegment(sketch, "E81", {"start": v(-33, 74.25) * mm, "end": v(-15, 92.25) * mm});
            skLineSegment(sketch, "E82", {"start": v(-15, 92.25) * mm, "end": v(-15, 104.25) * mm});
            skCircle(sketch, "E83", {"center": v(0, 104.25) * mm, "radius": 6 * mm});
            skArc(sketch, "E84", {"start": v(-15, 104.25) * mm, "mid": v(0, 119.25) * mm, "end": v(15, 104.25) * mm});
            skLineSegment(sketch, "E85", {"start": v(15, 104.25) * mm, "end": v(15, 92.25) * mm});
            skLineSegment(sketch, "E86", {"start": v(15, 92.25) * mm, "end": v(33, 74.25) * mm});
            skLineSegment(sketch, "E87", {"start": v(0, 0) * mm, "end": v(-74.25, 0) * mm, "construction": true});
            skLineSegment(sketch, "E88.MirrorCS", {"start": v(0, 0) * mm, "end": v(74.25, 0) * mm, "construction": true});
            skLineSegment(sketch, "E89", {"start": v(-74.25, 0) * mm, "end": v(74.25, 0) * mm, "construction": true});
            skLineSegment(sketch, "E90.MirrorCS", {"start": v(15, -92.25) * mm, "end": v(33, -74.25) * mm});
            skLineSegment(sketch, "E91.MirrorCS", {"start": v(15, -104.25) * mm, "end": v(15, -92.25) * mm});
            skCircle(sketch, "E92.MirrorC", {"center": v(0, -104.25) * mm, "radius": 6 * mm});
            skArc(sketch, "E93.MirrorCS", {"start": v(-15, -104.25) * mm, "mid": v(0, -119.25) * mm, "end": v(15, -104.25) * mm});
            skLineSegment(sketch, "E94.MirrorCS", {"start": v(-33, -74.25) * mm, "end": v(-15, -92.25) * mm});
            skLineSegment(sketch, "E95.MirrorCS", {"start": v(-15, -92.25) * mm, "end": v(-15, -104.25) * mm});
            skSolve(sketch);
        }
        {
            var Q0;
            {var subQ0=sQuery(id+"F16.wireOp",EDGE,"E81");Q0=makeQuery(id+"F16.imprint","IMPRINT",FACE,{"disambiguationData":[TD([[makeQuery(id+"F16.imprint","IMPRINT",EDGE,{"derivedFrom":subQ0}),-1.0]])]});}
            var Q1;
            Q1=makeQuery(id+"F16.imprint","IMPRINT",FACE,{"disambiguationData":[TD([[makeQuery(id+"F16.imprint","IMPRINT",EDGE,{"derivedFrom":sQuery(id+"F16.wireOp",EDGE,"E79.0")}),-1.0]])]});
            var Q2;
            {var subQ0=sQuery(id+"F16.wireOp",EDGE,"E90.MirrorCS");Q2=makeQuery(id+"F16.imprint","IMPRINT",FACE,{"disambiguationData":[TD([[makeQuery(id+"F16.imprint","IMPRINT",EDGE,{"derivedFrom":subQ0}),1.0]])]});}
            var Q3;
            Q3=makeQuery(id+"F2.opExtrude","CAP_FACE",FACE,{"disambiguationData":[OSD([sQuery(id+"F0.wireOp",EDGE,"E12"),sQuery(id+"F0.wireOp",EDGE,"E13"),sQuery(id+"F0.wireOp",EDGE,"E14"),sQuery(id+"F0.wireOp",EDGE,"E15"),sQuery(id+"F0.wireOp",EDGE,"E17.filletArc"),sQuery(id+"F0.wireOp",EDGE,"E18.filletArc"),sQuery(id+"F0.wireOp",EDGE,"E19.filletArc"),sQuery(id+"F0.wireOp",EDGE,"E20.filletArc"),sQuery(id+"F0.wireOp",EDGE,"E25.0"),sQuery(id+"F0.wireOp",EDGE,"E25.1"),sQuery(id+"F0.wireOp",EDGE,"E25.2"),sQuery(id+"F0.wireOp",EDGE,"E25.3"),sQuery(id+"F0.wireOp",EDGE,"E25.4"),sQuery(id+"F0.wireOp",EDGE,"E25.5"),sQuery(id+"F0.wireOp",EDGE,"E25.6"),sQuery(id+"F0.wireOp",EDGE,"E25.7")])],"isStart":false});
            extrude(context, id + "F17", {"entities" : qUnion([Q0, Q1, Q2]), "endBound" : BoundingType.UP_TO_SURFACE, "depth" : 25 * mm, "endBoundEntityFace" : qUnion([Q3]), "offsetDistance" : 25 * mm});
        }
    });
